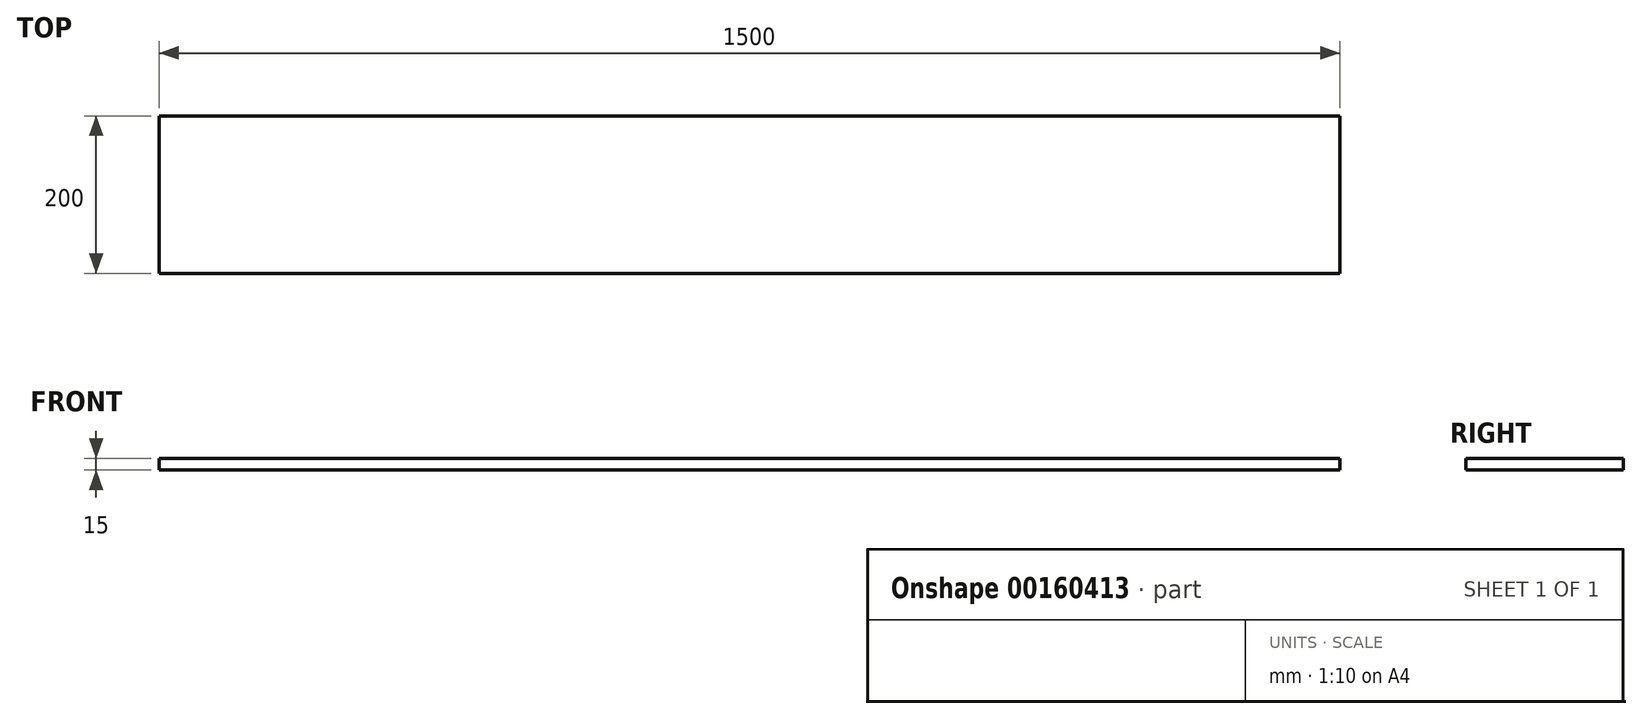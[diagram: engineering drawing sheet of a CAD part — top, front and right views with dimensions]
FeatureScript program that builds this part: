
annotation { "Feature Type Name" : "Feature", "Feature Type Description" : "" }
export const myFeature = defineFeature(function(context is Context, id is Id, definition is map)
    precondition{}
    {
        {
            var Q0;
            Q0=qCreatedBy(makeId("Top.planeOp"),FACE);
            var sketch = newSketch(context, id + "F0", { "sketchPlane" : qUnion([Q0])});
            skLineSegment(sketch, "E0.bottom", {"start": v(-516.87, -72.16) * mm, "end": v(983.13, -72.16) * mm});
            skLineSegment(sketch, "E0.top", {"start": v(-516.87, -272.16) * mm, "end": v(983.13, -272.16) * mm});
            skLineSegment(sketch, "E0.left", {"start": v(-516.87, -72.16) * mm, "end": v(-516.87, -272.16) * mm});
            skLineSegment(sketch, "E0.right", {"start": v(983.13, -72.16) * mm, "end": v(983.13, -272.16) * mm});
            skSolve(sketch);
        }
        {
            var Q0;
            Q0=makeQuery(id+"F0.imprint","IMPRINT",FACE,{"disambiguationData":[TD([[makeQuery(id+"F0.imprint","IMPRINT",EDGE,{"derivedFrom":sQuery(id+"F0.wireOp",EDGE,"E0.bottom")}),-1.0]])]});
            extrude(context, id + "F1", {"entities" : qUnion([Q0]), "depth" : 15 * mm});
        }
    });
